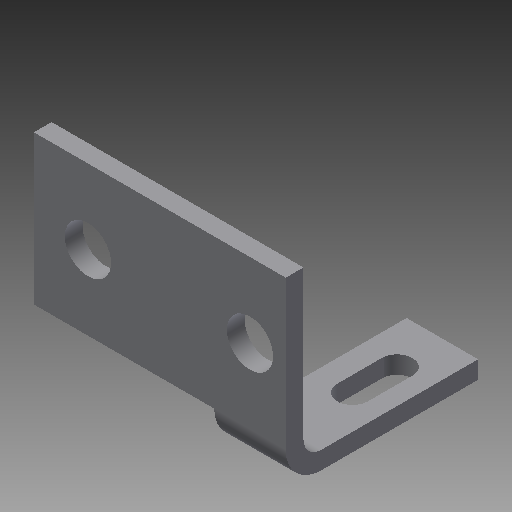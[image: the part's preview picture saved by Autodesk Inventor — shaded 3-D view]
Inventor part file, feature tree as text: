
AUTODESK INVENTOR PART (.ipt)
format: ipt  version: 2017 (Build 210142000, 142)  size: 148,480 bytes
history: native  units: in
note: dims shown in document units (in); Inventor stores cm internally (conversion verified against a paired STEP export)
features: sketch x5, sheet_metal_op x4, extrude x3, other x2
ambient origin geometry x8: Origin, YZ Plane, XZ Plane, XY Plane, X Axis, Y Axis, Z Axis, Center Point
bodies: Body1 (feature_tree)
feature tree (14):
  sheet_metal_op  "Face1"
  sheet_metal_op  "Flange1"
  extrude  "Extrusion3"  Depth=0.238in
  extrude  "Extrusion4"  Depth=0.305in
  extrude  "Extrusion5"  Depth=0.125in
  sketch  "Sketch1"  dims[d0=0.64in d1=0.238in]
  other  "Plate1"
  sketch  "Sketch2"  dims[d2=0.157in d3=0.305in]
  other  "Plate2"
  sheet_metal_op  "Bend1"
  sheet_metal_op  "Corner1"
  sketch  "Sketch4"  dims[d4=0.125in d5=0.125in]
  sketch  "Sketch5"  dims[d10=0.059in]
  sketch  "Sketch6"  dims[d11=0.059in d12=0.0295in d13=0.118in d14=0.059in d15=0.614in d16=90.0deg d17=0.059in d18=0.236in d19=0.059in d20=0.059in d21=0.248in d22=0.154in d23=0.059in d24=0.0in d25=0.6in d26=0.0in d27=0.18in d28=0.248in d29=0.154in d30=0.375in d31=0.0in]
